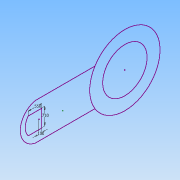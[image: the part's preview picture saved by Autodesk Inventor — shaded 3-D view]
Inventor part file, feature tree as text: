
AUTODESK INVENTOR PART (.ipt)
format: ipt  version: 2015 (Build 190159000, 159)  size: 64,512 bytes
history: native  units: in
note: dims shown in document units (in); Inventor stores cm internally (conversion verified against a paired STEP export)
features: sketch x1
ambient origin geometry x8: Origin, YZ Plane, XZ Plane, XY Plane, X Axis, Y Axis, Z Axis, Center Point
feature tree (1):
  sketch  "Sketch1"  dims[d0=0.71in d1=0.55in d2=0.1in]
